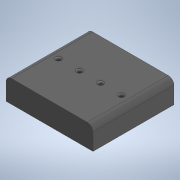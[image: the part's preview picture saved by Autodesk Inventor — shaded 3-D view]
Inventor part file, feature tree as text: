
AUTODESK INVENTOR PART (.ipt)
format: ipt  version: 2020 (Build 240168000, 168)  size: 113,664 bytes
history: native  units: mm
features: extrude x2, sketch x2
ambient origin geometry x8: Origin, YZ Plane, XZ Plane, XY Plane, X Axis, Y Axis, Z Axis, Center Point
bodies: Solid1 (feature_tree)
feature tree (4):
  extrude  "Extrusion1"  Depth=62.0mm
  extrude  "Extrusion2"  Depth=57.7mm TaperAngle=0.0deg
  sketch  "Sketch1"  dims[d0=16.0mm d1=62.0mm]
  sketch  "Sketch2"  dims[d2=4.0mm d3=57.7mm d4=0.0mm d5=45.0mm d8=4.0mm d9=15.0mm d10=0.0mm d11=0.0mm]
